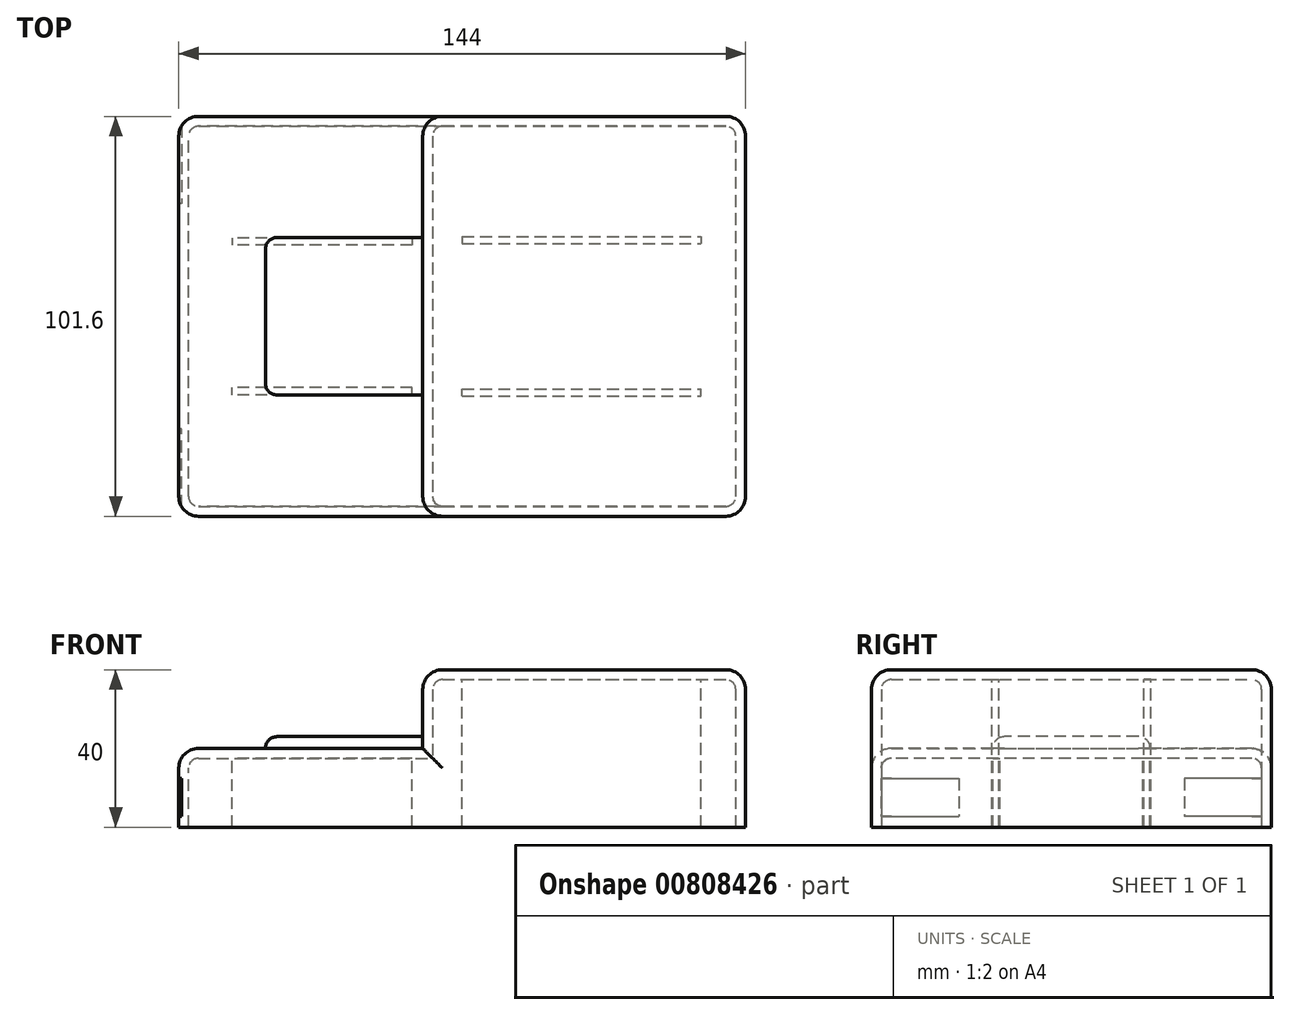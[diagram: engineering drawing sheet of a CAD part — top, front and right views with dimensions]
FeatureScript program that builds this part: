
annotation { "Feature Type Name" : "Feature", "Feature Type Description" : "" }
export const myFeature = defineFeature(function(context is Context, id is Id, definition is map)
    precondition{}
    {
        {
            var Q0;
            Q0=qCreatedBy(makeId("Top.planeOp"),FACE);
            var sketch = newSketch(context, id + "F0", { "sketchPlane" : qUnion([Q0])});
            skLineSegment(sketch, "E0.bottom", {"start": v(72, -50.8) * mm, "end": v(-72, -50.8) * mm});
            skLineSegment(sketch, "E0.top", {"start": v(72, 50.8) * mm, "end": v(-72, 50.8) * mm});
            skLineSegment(sketch, "E0.left", {"start": v(72, -50.8) * mm, "end": v(72, 50.8) * mm});
            skLineSegment(sketch, "E0.right", {"start": v(-72, -50.8) * mm, "end": v(-72, 50.8) * mm});
            skPoint(sketch, "E0.middle", {"position": v(0, 0) * mm});
            skSolve(sketch);
        }
        {
            var Q0;
            Q0=makeQuery(id+"F0.imprint","IMPRINT",FACE,{"disambiguationData":[TD([[makeQuery(id+"F0.imprint","IMPRINT",EDGE,{"derivedFrom":sQuery(id+"F0.wireOp",EDGE,"E0.bottom")}),-1.0]])]});
            extrude(context, id + "F1", {"entities" : qUnion([Q0]), "depth" : 20 * mm, "offsetDistance" : 25 * mm});
        }
        {
            var Q0;
            Q0=makeQuery(id+"F1.opExtrude","CAP_FACE",FACE,{"disambiguationData":[OSD([sQuery(id+"F0.wireOp",EDGE,"E0.bottom"),sQuery(id+"F0.wireOp",EDGE,"E0.top"),sQuery(id+"F0.wireOp",EDGE,"E0.left"),sQuery(id+"F0.wireOp",EDGE,"E0.right")])],"isStart":false});
            var sketch = newSketch(context, id + "F2", { "sketchPlane" : qUnion([Q0])});
            skLineSegment(sketch, "E1.bottom", {"start": v(72, 50.8) * mm, "end": v(-10, 50.8) * mm});
            skLineSegment(sketch, "E1.top", {"start": v(72, -50.8) * mm, "end": v(-10, -50.8) * mm});
            skLineSegment(sketch, "E1.left", {"start": v(72, 50.8) * mm, "end": v(72, -50.8) * mm});
            skLineSegment(sketch, "E1.right", {"start": v(-10, 50.8) * mm, "end": v(-10, -50.8) * mm});
            skSolve(sketch);
        }
        {
            var Q0;
            Q0=makeQuery(id+"F2.imprint","IMPRINT",FACE,{"disambiguationData":[TD([[makeQuery(id+"F2.imprint","IMPRINT",EDGE,{"derivedFrom":sQuery(id+"F2.wireOp",EDGE,"E1.bottom")}),1.0]])]});
            var Q1;
            Q1 = qSketchRegion(id + "F2", true);
            extrude(context, id + "F3", {"entities" : qUnion([Q0, Q1]), "operationType" : NewBodyOperationType.ADD, "depth" : 20 * mm, "offsetDistance" : 25 * mm});
        }
        {
            var Q0;
            Q0=makeQuery(id+"F1.opExtrude","CAP_EDGE",EDGE,{"disambiguationData":[OSD([sQuery(id+"F0.wireOp",EDGE,"E0.right")])],"isStart":false});
            var Q1;
            Q1=makeQuery(id+"F1.opExtrude","CAP_EDGE",EDGE,{"disambiguationData":[OSD([sQuery(id+"F0.wireOp",EDGE,"E0.bottom")])],"isStart":false});
            var Q2;
            Q2=makeQuery(id+"F3.opExtrude","SWEPT_EDGE",EDGE,{"disambiguationData":[OSD([sQuery(id+"F0.wireOp",EDGE,"E0.bottom"),sQuery(id+"F2.wireOp",EDGE,"E1.top"),sQuery(id+"F2.wireOp",EDGE,"E1.right")])]});
            var Q3;
            Q3=makeQuery(id+"F3.opExtrude","CAP_EDGE",EDGE,{"disambiguationData":[OSD([sQuery(id+"F2.wireOp",EDGE,"E1.top")])],"isStart":false});
            var Q4;
            Q4=makeQuery(id+"F3.opExtrude","CAP_EDGE",EDGE,{"disambiguationData":[OSD([sQuery(id+"F2.wireOp",EDGE,"E1.bottom")])],"isStart":false});
            var Q5;
            Q5=makeQuery(id+"F1.opExtrude","CAP_EDGE",EDGE,{"disambiguationData":[OSD([sQuery(id+"F0.wireOp",EDGE,"E0.top")])],"isStart":false});
            var Q6;
            Q6=makeQuery(id+"F3.opExtrude","SWEPT_EDGE",EDGE,{"disambiguationData":[OSD([sQuery(id+"F0.wireOp",EDGE,"E0.top"),sQuery(id+"F2.wireOp",EDGE,"E1.bottom"),sQuery(id+"F2.wireOp",EDGE,"E1.right")])]});
            var Q7;
            Q7=makeQuery(id+"F1.opExtrude","SWEPT_EDGE",EDGE,{"disambiguationData":[OSD([sQuery(id+"F0.wireOp",EDGE,"E0.top"),sQuery(id+"F0.wireOp",EDGE,"E0.right")])]});
            var Q8;
            Q8=makeQuery(id+"F1.opExtrude","SWEPT_EDGE",EDGE,{"disambiguationData":[OSD([sQuery(id+"F0.wireOp",EDGE,"E0.bottom"),sQuery(id+"F0.wireOp",EDGE,"E0.right")])]});
            var Q9;
            Q9=makeQuery(id+"F3.boolean.opBoolean","MERGE",EDGE,{"derivedFrom":[makeQuery(id+"F1.opExtrude","SWEPT_EDGE",EDGE,{"disambiguationData":[OSD([sQuery(id+"F0.wireOp",EDGE,"E0.bottom"),sQuery(id+"F0.wireOp",EDGE,"E0.left")])]}),makeQuery(id+"F3.opExtrude","SWEPT_EDGE",EDGE,{"disambiguationData":[OSD([sQuery(id+"F2.wireOp",EDGE,"E1.top"),sQuery(id+"F2.wireOp",EDGE,"E1.left")])]})]});
            var Q10;
            Q10=makeQuery(id+"F3.boolean.opBoolean","MERGE",EDGE,{"derivedFrom":[makeQuery(id+"F1.opExtrude","SWEPT_EDGE",EDGE,{"disambiguationData":[OSD([sQuery(id+"F0.wireOp",EDGE,"E0.top"),sQuery(id+"F0.wireOp",EDGE,"E0.left")])]}),makeQuery(id+"F3.opExtrude","SWEPT_EDGE",EDGE,{"disambiguationData":[OSD([sQuery(id+"F2.wireOp",EDGE,"E1.bottom"),sQuery(id+"F2.wireOp",EDGE,"E1.left")])]})]});
            var Q11;
            Q11=makeQuery(id+"F3.opExtrude","CAP_EDGE",EDGE,{"disambiguationData":[OSD([sQuery(id+"F2.wireOp",EDGE,"E1.left")])],"isStart":false});
            var Q12;
            Q12=makeQuery(id+"F3.opExtrude","CAP_EDGE",EDGE,{"disambiguationData":[OSD([sQuery(id+"F2.wireOp",EDGE,"E1.right")])],"isStart":false});
            fillet(context, id + "F4", {"entities" : qUnion([Q0, Q1, Q2, Q3, Q4, Q5, Q6, Q7, Q8, Q9, Q10, Q11, Q12]), "radius" : 5 * mm, "tangentPropagation" : true, "allowEdgeOverflow" : false});
        }
        {
            var Q0;
            Q0=makeQuery(id+"F1.opExtrude","CAP_FACE",FACE,{"disambiguationData":[OSD([sQuery(id+"F0.wireOp",EDGE,"E0.bottom"),sQuery(id+"F0.wireOp",EDGE,"E0.top"),sQuery(id+"F0.wireOp",EDGE,"E0.left"),sQuery(id+"F0.wireOp",EDGE,"E0.right")])],"isStart":true});
            shell(context, id + "F5", {"entities" : qUnion([Q0]), "thickness" : 2.5 * mm});
        }
        {
            var Q0;
            Q0=makeQuery(id+"F5.opShell","OFFSET_FACE",FACE,{"disambiguationData":[OSD([sQuery(id+"F2.wireOp",EDGE,"E1.bottom"),sQuery(id+"F2.wireOp",EDGE,"E1.top"),sQuery(id+"F2.wireOp",EDGE,"E1.left"),sQuery(id+"F2.wireOp",EDGE,"E1.right")])]});
            var sketch = newSketch(context, id + "F6", { "sketchPlane" : qUnion([Q0])});
            skLineSegment(sketch, "E2.bottom", {"start": v(0, 20.22) * mm, "end": v(60.67, 20.22) * mm});
            skLineSegment(sketch, "E2.top", {"start": v(0, 17.42) * mm, "end": v(60.67, 17.42) * mm});
            skLineSegment(sketch, "E2.left", {"start": v(0, 20.22) * mm, "end": v(0, 17.42) * mm});
            skLineSegment(sketch, "E2.right", {"start": v(60.67, 20.22) * mm, "end": v(60.67, 17.42) * mm});
            skLineSegment(sketch, "E3.MirrorCS", {"start": v(0, -20.22) * mm, "end": v(0, -17.42) * mm});
            skLineSegment(sketch, "E4.MirrorCS", {"start": v(0, -17.42) * mm, "end": v(60.67, -17.42) * mm});
            skLineSegment(sketch, "E5.MirrorCS", {"start": v(0, -20.22) * mm, "end": v(60.67, -20.22) * mm});
            skLineSegment(sketch, "E6.MirrorCS", {"start": v(60.67, -20.22) * mm, "end": v(60.67, -17.42) * mm});
            skSolve(sketch);
        }
        {
            var Q0;
            Q0=makeQuery(id+"F5.opShell","OFFSET_FACE",FACE,{"disambiguationData":[OSD([sQuery(id+"F0.wireOp",EDGE,"E0.bottom"),sQuery(id+"F0.wireOp",EDGE,"E0.top"),sQuery(id+"F0.wireOp",EDGE,"E0.left"),sQuery(id+"F0.wireOp",EDGE,"E0.right")])]});
            var sketch = newSketch(context, id + "F7", { "sketchPlane" : qUnion([Q0])});
            skLineSegment(sketch, "E7.bottom", {"start": v(-12.72, 19.94) * mm, "end": v(-58.4, 19.94) * mm});
            skLineSegment(sketch, "E7.top", {"start": v(-12.72, 17.15) * mm, "end": v(-58.4, 17.15) * mm});
            skLineSegment(sketch, "E7.left", {"start": v(-12.72, 19.94) * mm, "end": v(-12.72, 17.15) * mm});
            skLineSegment(sketch, "E7.right", {"start": v(-58.4, 19.94) * mm, "end": v(-58.4, 17.15) * mm});
            skLineSegment(sketch, "E8.MirrorCS", {"start": v(-12.72, -19.94) * mm, "end": v(-58.4, -19.94) * mm});
            skLineSegment(sketch, "E9.MirrorCS", {"start": v(-12.72, -17.15) * mm, "end": v(-58.4, -17.15) * mm});
            skLineSegment(sketch, "E10.MirrorCS", {"start": v(-12.72, -19.94) * mm, "end": v(-12.72, -17.15) * mm});
            skLineSegment(sketch, "E11.MirrorCS", {"start": v(-58.4, -19.94) * mm, "end": v(-58.4, -17.15) * mm});
            skSolve(sketch);
        }
        {
            var Q0;
            Q0=makeQuery(id+"F7.imprint","IMPRINT",FACE,{"disambiguationData":[TD([[makeQuery(id+"F7.imprint","IMPRINT",EDGE,{"derivedFrom":sQuery(id+"F7.wireOp",EDGE,"E7.bottom")}),1.0]])]});
            var Q1;
            Q1=makeQuery(id+"F7.imprint","IMPRINT",FACE,{"disambiguationData":[TD([[makeQuery(id+"F7.imprint","IMPRINT",EDGE,{"derivedFrom":sQuery(id+"F7.wireOp",EDGE,"E8.MirrorCS")}),-1.0]])]});
            extrude(context, id + "F8", {"entities" : qUnion([Q0, Q1]), "operationType" : NewBodyOperationType.ADD, "depth" : 17.5 * mm, "offsetDistance" : 25 * mm});
        }
        {
            var Q0;
            Q0=makeQuery(id+"F6.imprint","IMPRINT",FACE,{"disambiguationData":[TD([[makeQuery(id+"F6.imprint","IMPRINT",EDGE,{"derivedFrom":sQuery(id+"F6.wireOp",EDGE,"E2.bottom")}),-1.0]])]});
            var Q1;
            Q1=makeQuery(id+"F6.imprint","IMPRINT",FACE,{"disambiguationData":[TD([[makeQuery(id+"F6.imprint","IMPRINT",EDGE,{"derivedFrom":sQuery(id+"F6.wireOp",EDGE,"E3.MirrorCS")}),-1.0]])]});
            extrude(context, id + "F9", {"entities" : qUnion([Q0, Q1]), "operationType" : NewBodyOperationType.ADD, "depth" : 37.5 * mm, "offsetDistance" : 25 * mm});
        }
        {
            var Q0;
            Q0=makeQuery(id+"F8.opExtrude","SWEPT_FACE",FACE,{"disambiguationData":[OSD([sQuery(id+"F7.wireOp",EDGE,"E9.MirrorCS")])]});
            var Q1;
            Q1=makeQuery(id+"F9.opExtrude","SWEPT_FACE",FACE,{"disambiguationData":[OSD([sQuery(id+"F6.wireOp",EDGE,"E4.MirrorCS")])]});
            extrude(context, id + "F10", {"entities" : qUnion([Q0, Q1]), "operationType" : NewBodyOperationType.REMOVE, "oppositeDirection" : true, "depth" : 1 * mm, "offsetDistance" : 25 * mm});
        }
        {
            var Q0;
            Q0=makeQuery(id+"F9.opExtrude","SWEPT_FACE",FACE,{"disambiguationData":[OSD([sQuery(id+"F6.wireOp",EDGE,"E2.top")])]});
            var Q1;
            Q1=makeQuery(id+"F8.opExtrude","SWEPT_FACE",FACE,{"disambiguationData":[OSD([sQuery(id+"F7.wireOp",EDGE,"E7.top")])]});
            extrude(context, id + "F11", {"entities" : qUnion([Q0, Q1]), "operationType" : NewBodyOperationType.REMOVE, "oppositeDirection" : true, "depth" : 1 * mm, "offsetDistance" : 25 * mm});
        }
        {
            var Q0;
            Q0=makeQuery(id+"F1.opExtrude","SWEPT_FACE",FACE,{"disambiguationData":[OSD([sQuery(id+"F0.wireOp",EDGE,"E0.right")])]});
            var sketch = newSketch(context, id + "F12", { "sketchPlane" : qUnion([Q0])});
            skLineSegment(sketch, "E12.bottom", {"start": v(-52.19, 12.4) * mm, "end": v(-28.64, 12.4) * mm});
            skLineSegment(sketch, "E12.top", {"start": v(-52.19, 2.78) * mm, "end": v(-28.64, 2.78) * mm});
            skLineSegment(sketch, "E12.left", {"start": v(-52.19, 12.4) * mm, "end": v(-52.19, 2.78) * mm});
            skLineSegment(sketch, "E12.right", {"start": v(-28.64, 12.4) * mm, "end": v(-28.64, 2.78) * mm});
            skLineSegment(sketch, "E13.MirrorCS", {"start": v(52.19, 12.4) * mm, "end": v(28.64, 12.4) * mm});
            skLineSegment(sketch, "E14.MirrorCS", {"start": v(52.19, 2.78) * mm, "end": v(28.64, 2.78) * mm});
            skLineSegment(sketch, "E15.MirrorCS", {"start": v(52.19, 12.4) * mm, "end": v(52.19, 2.78) * mm});
            skLineSegment(sketch, "E16.MirrorCS", {"start": v(28.64, 12.4) * mm, "end": v(28.64, 2.78) * mm});
            skSolve(sketch);
        }
        {
            var Q0;
            Q0=makeQuery(id+"F12.imprint","IMPRINT",FACE,{"disambiguationData":[TD([[makeQuery(id+"F12.imprint","IMPRINT",EDGE,{"derivedFrom":sQuery(id+"F12.wireOp",EDGE,"E13.MirrorCS")}),1.0]])]});
            var Q1;
            Q1=makeQuery(id+"F12.imprint","IMPRINT",FACE,{"disambiguationData":[TD([[makeQuery(id+"F12.imprint","IMPRINT",EDGE,{"derivedFrom":sQuery(id+"F12.wireOp",EDGE,"E12.bottom")}),-1.0]])]});
            extrude(context, id + "F13", {"entities" : qUnion([Q0, Q1]), "operationType" : NewBodyOperationType.REMOVE, "oppositeDirection" : true, "depth" : 0.7 * mm, "offsetDistance" : 25 * mm});
        }
        {
            var Q0;
            Q0=makeQuery(id+"F1.opExtrude","CAP_FACE",FACE,{"disambiguationData":[OSD([sQuery(id+"F0.wireOp",EDGE,"E0.bottom"),sQuery(id+"F0.wireOp",EDGE,"E0.top"),sQuery(id+"F0.wireOp",EDGE,"E0.left"),sQuery(id+"F0.wireOp",EDGE,"E0.right")])],"isStart":false});
            var sketch = newSketch(context, id + "F14", { "sketchPlane" : qUnion([Q0])});
            skLineSegment(sketch, "E17.bottom", {"start": v(-10, -20) * mm, "end": v(-50, -20) * mm});
            skLineSegment(sketch, "E17.top", {"start": v(-10, 20) * mm, "end": v(-50, 20) * mm});
            skLineSegment(sketch, "E17.left", {"start": v(-10, -20) * mm, "end": v(-10, 20) * mm});
            skLineSegment(sketch, "E17.right", {"start": v(-50, -20) * mm, "end": v(-50, 20) * mm});
            skPoint(sketch, "E17.middle", {"position": v(-30, 0) * mm});
            skSolve(sketch);
        }
        {
            var Q0;
            Q0=makeQuery(id+"F14.imprint","IMPRINT",FACE,{"disambiguationData":[TD([[makeQuery(id+"F14.imprint","IMPRINT",EDGE,{"derivedFrom":sQuery(id+"F14.wireOp",EDGE,"E17.bottom")}),-1.0]])]});
            extrude(context, id + "F15", {"entities" : qUnion([Q0]), "operationType" : NewBodyOperationType.ADD, "depth" : 3 * mm, "offsetDistance" : 25 * mm});
        }
        {
            var Q0;
            Q0=makeQuery(id+"F15.opExtrude","SWEPT_EDGE",EDGE,{"disambiguationData":[OSD([sQuery(id+"F14.wireOp",EDGE,"E17.bottom"),sQuery(id+"F14.wireOp",EDGE,"E17.right")])]});
            var Q1;
            Q1=makeQuery(id+"F15.opExtrude","CAP_EDGE",EDGE,{"disambiguationData":[OSD([sQuery(id+"F14.wireOp",EDGE,"E17.bottom")])],"isStart":false});
            var Q2;
            Q2=makeQuery(id+"F15.opExtrude","CAP_EDGE",EDGE,{"disambiguationData":[OSD([sQuery(id+"F14.wireOp",EDGE,"E17.top")])],"isStart":false});
            var Q3;
            Q3=makeQuery(id+"F15.opExtrude","SWEPT_EDGE",EDGE,{"disambiguationData":[OSD([sQuery(id+"F14.wireOp",EDGE,"E17.top"),sQuery(id+"F14.wireOp",EDGE,"E17.right")])]});
            var Q4;
            Q4=makeQuery(id+"F15.opExtrude","CAP_EDGE",EDGE,{"disambiguationData":[OSD([sQuery(id+"F14.wireOp",EDGE,"E17.right")])],"isStart":false});
            fillet(context, id + "F16", {"entities" : qUnion([Q0, Q1, Q2, Q3, Q4]), "radius" : 3 * mm, "tangentPropagation" : true, "allowEdgeOverflow" : false});
        }
    });
